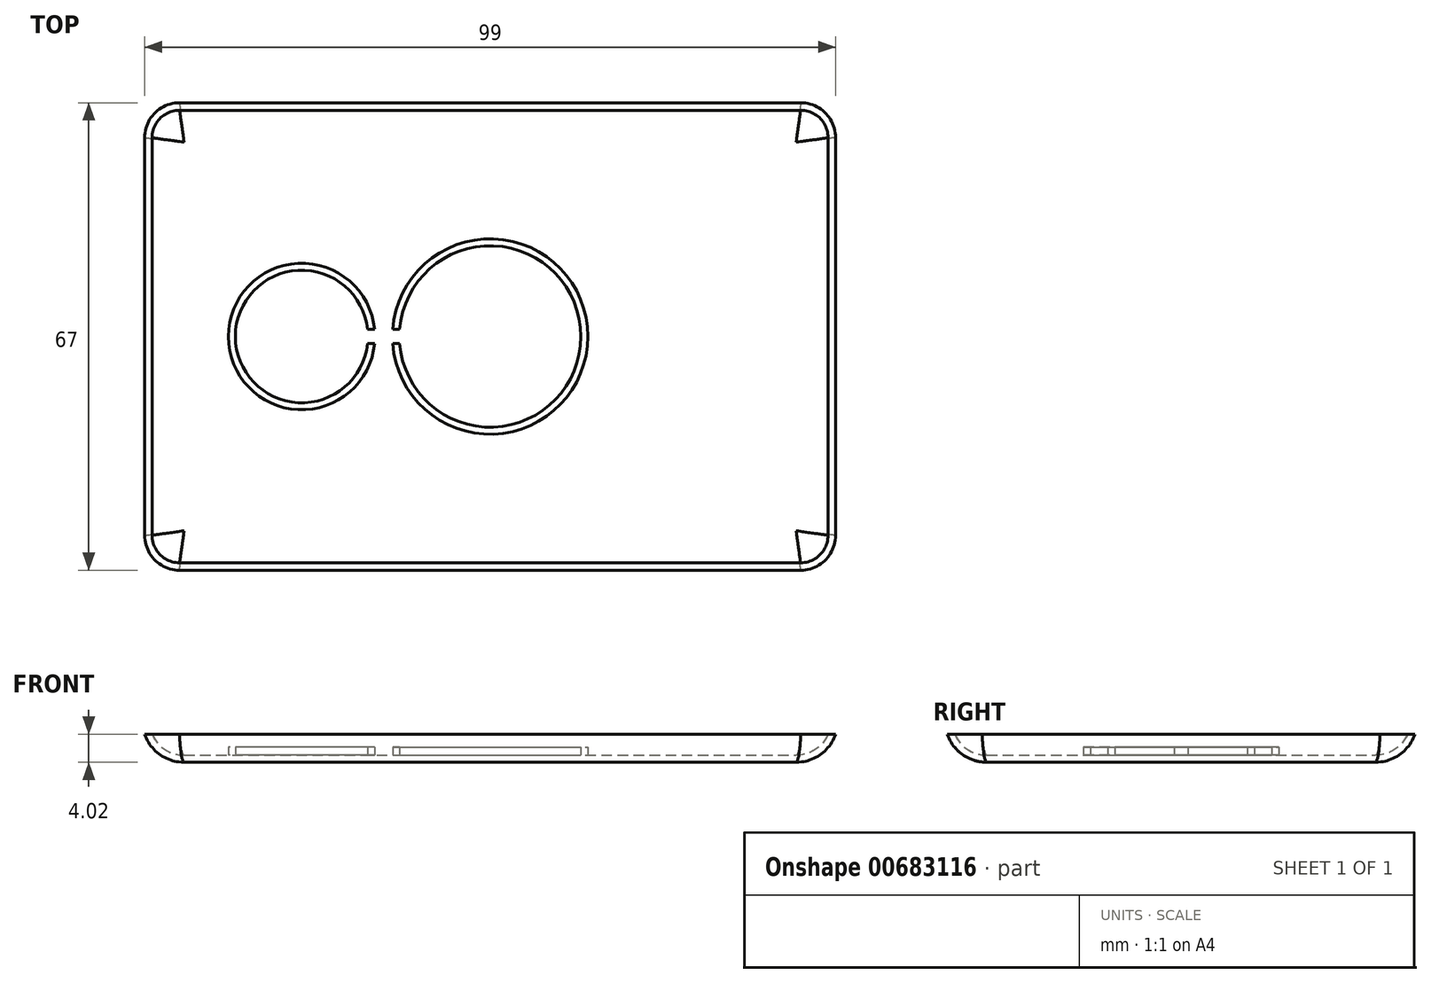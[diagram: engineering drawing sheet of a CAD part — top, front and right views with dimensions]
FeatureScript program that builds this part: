
annotation { "Feature Type Name" : "Feature", "Feature Type Description" : "" }
export const myFeature = defineFeature(function(context is Context, id is Id, definition is map)
    precondition{}
    {
        {
            var Q0;
            Q0=qCreatedBy(makeId("Top.planeOp"),FACE);
            var sketch = newSketch(context, id + "F0", { "sketchPlane" : qUnion([Q0])});
            skLineSegment(sketch, "E0.bottom", {"start": v(-44.5, 33.5) * mm, "end": v(44.5, 33.5) * mm});
            skLineSegment(sketch, "E0.top", {"start": v(-44.5, -33.5) * mm, "end": v(44.5, -33.5) * mm});
            skLineSegment(sketch, "E0.left", {"start": v(-49.5, 28.5) * mm, "end": v(-49.5, -28.5) * mm});
            skLineSegment(sketch, "E0.right", {"start": v(49.5, 28.5) * mm, "end": v(49.5, -28.5) * mm});
            skPoint(sketch, "E1", {"position": v(0, 33.5) * mm});
            skPoint(sketch, "E2", {"position": v(49.5, 0) * mm});
            skPoint(sketch, "E3", {"position": v(0, -33.5) * mm});
            skPoint(sketch, "E4", {"position": v(-49.5, 0) * mm});
            skPoint(sketch, "E5.visualSharp", {"position": v(-49.5, 33.5) * mm});
            skArc(sketch, "E5.filletArc", {"start": v(-44.5, 33.5) * mm, "mid": v(-48.04, 32.04) * mm, "end": v(-49.5, 28.5) * mm});
            skPoint(sketch, "E6.visualSharp", {"position": v(49.5, 33.5) * mm});
            skArc(sketch, "E6.filletArc", {"start": v(49.5, 28.5) * mm, "mid": v(48.04, 32.04) * mm, "end": v(44.5, 33.5) * mm});
            skPoint(sketch, "E7.visualSharp", {"position": v(49.5, -33.5) * mm});
            skArc(sketch, "E7.filletArc", {"start": v(44.5, -33.5) * mm, "mid": v(48.04, -32.04) * mm, "end": v(49.5, -28.5) * mm});
            skPoint(sketch, "E8.visualSharp", {"position": v(-49.5, -33.5) * mm});
            skArc(sketch, "E8.filletArc", {"start": v(-49.5, -28.5) * mm, "mid": v(-48.04, -32.04) * mm, "end": v(-44.5, -33.5) * mm});
            skSolve(sketch);
        }
        {
            var Q0;
            Q0 = qSketchRegion(id + "F0", true);
            extrude(context, id + "F1", {"entities" : qUnion([Q0]), "depth" : 4 * mm, "offsetDistance" : 25.4 * mm});
        }
        {
            var Q0;
            Q0=makeQuery(id+"F1.opExtrude","CAP_EDGE",EDGE,{"disambiguationData":[OSD([sQuery(id+"F0.wireOp",EDGE,"C0Ow9CS6-q4R2-3ig4-oCDO-nPJFPDyijR1C.bottom")])],"isStart":true});
            var Q1;
            Q1=makeQuery(id+"F1.opExtrude","CAP_EDGE",EDGE,{"disambiguationData":[OSD([sQuery(id+"F0.wireOp",EDGE,"E0.top")])],"isStart":true});
            fillet(context, id + "F2", {"entities" : qUnion([Q0, Q1]), "radius" : 6 * mm, "tangentPropagation" : true, "allowEdgeOverflow" : false});
        }
        {
            var Q0;
            Q0=makeQuery(id+"F1.opExtrude","CAP_FACE",FACE,{"disambiguationData":[OSD([sQuery(id+"F0.wireOp",EDGE,"E0.bottom"),sQuery(id+"F0.wireOp",EDGE,"E0.top"),sQuery(id+"F0.wireOp",EDGE,"E0.left"),sQuery(id+"F0.wireOp",EDGE,"E0.right")])],"isStart":false});
            shell(context, id + "F3", {"entities" : qUnion([Q0]), "thickness" : 1 * mm});
        }
        {
            var Q0;
            Q0=makeQuery(id+"F3.opShell","OFFSET_FACE",FACE,{"disambiguationData":[OSD([sQuery(id+"F0.wireOp",EDGE,"E0.bottom"),sQuery(id+"F0.wireOp",EDGE,"E0.top"),sQuery(id+"F0.wireOp",EDGE,"E0.left"),sQuery(id+"F0.wireOp",EDGE,"E0.right"),sQuery(id+"F0.wireOp",EDGE,"E5.filletArc"),sQuery(id+"F0.wireOp",EDGE,"E6.filletArc"),sQuery(id+"F0.wireOp",EDGE,"E7.filletArc"),sQuery(id+"F0.wireOp",EDGE,"E8.filletArc")])]});
            var sketch = newSketch(context, id + "F4", { "sketchPlane" : qUnion([Q0])});
            skCircle(sketch, "E9", {"center": v(-27, 0) * mm, "radius": 9.5 * mm});
            skCircle(sketch, "E10", {"center": v(-27, 0) * mm, "radius": 10.5 * mm});
            skCircle(sketch, "E11", {"center": v(0, 0) * mm, "radius": 14 * mm});
            skCircle(sketch, "E12", {"center": v(0, 0) * mm, "radius": 13 * mm});
            skSolve(sketch);
        }
        {
            var Q0;
            Q0 = qSketchRegion(id + "F4", true);
            extrude(context, id + "F5", {"entities" : qUnion([Q0]), "operationType" : NewBodyOperationType.ADD, "depth" : 1.2 * mm, "offsetDistance" : 25 * mm});
        }
        {
            var Q0;
            {var subQ0=sQuery(id+"F0.wireOp",EDGE,"E0.right");var subQ1=sQuery(id+"F0.wireOp",EDGE,"E0.left");var subQ2=sQuery(id+"F0.wireOp",EDGE,"E0.top");var subQ3=sQuery(id+"F0.wireOp",EDGE,"E0.bottom");var subQ4=sQuery(id+"F0.wireOp",EDGE,"E5.filletArc");var subQ5=sQuery(id+"F0.wireOp",EDGE,"E6.filletArc");var subQ6=sQuery(id+"F0.wireOp",EDGE,"E7.filletArc");var subQ7=sQuery(id+"F0.wireOp",EDGE,"E8.filletArc");Q0=makeQuery(id+"F5.boolean.opBoolean","SPLIT",FACE,{"disambiguationData":[TD([makeQuery(id+"F5.opExtrude","SWEPT_FACE",FACE,{"disambiguationData":[OSD([sQuery(id+"F4.wireOp",EDGE,"E10")])]})])],"derivedFrom":makeQuery(id+"F3.opShell","OFFSET_FACE",FACE,{"disambiguationData":[OSD([subQ3,subQ2,subQ1,subQ0,subQ4,subQ5,subQ6,subQ7])]})});}
            var sketch = newSketch(context, id + "F6", { "sketchPlane" : qUnion([Q0])});
            skLineSegment(sketch, "E13.bottom", {"start": v(-18.5, 1) * mm, "end": v(-12, 1) * mm});
            skLineSegment(sketch, "E13.top", {"start": v(-18.5, -1) * mm, "end": v(-12, -1) * mm});
            skLineSegment(sketch, "E13.left", {"start": v(-18.5, 1) * mm, "end": v(-18.5, -1) * mm});
            skLineSegment(sketch, "E13.right", {"start": v(-12, 1) * mm, "end": v(-12, -1) * mm});
            skPoint(sketch, "E14", {"position": v(-12, 0) * mm});
            skSolve(sketch);
        }
        {
            var Q0;
            Q0 = qSketchRegion(id + "F6", true);
            extrude(context, id + "F7", {"entities" : qUnion([Q0]), "operationType" : NewBodyOperationType.REMOVE, "depth" : 25 * mm, "offsetDistance" : 25 * mm});
        }
    });
